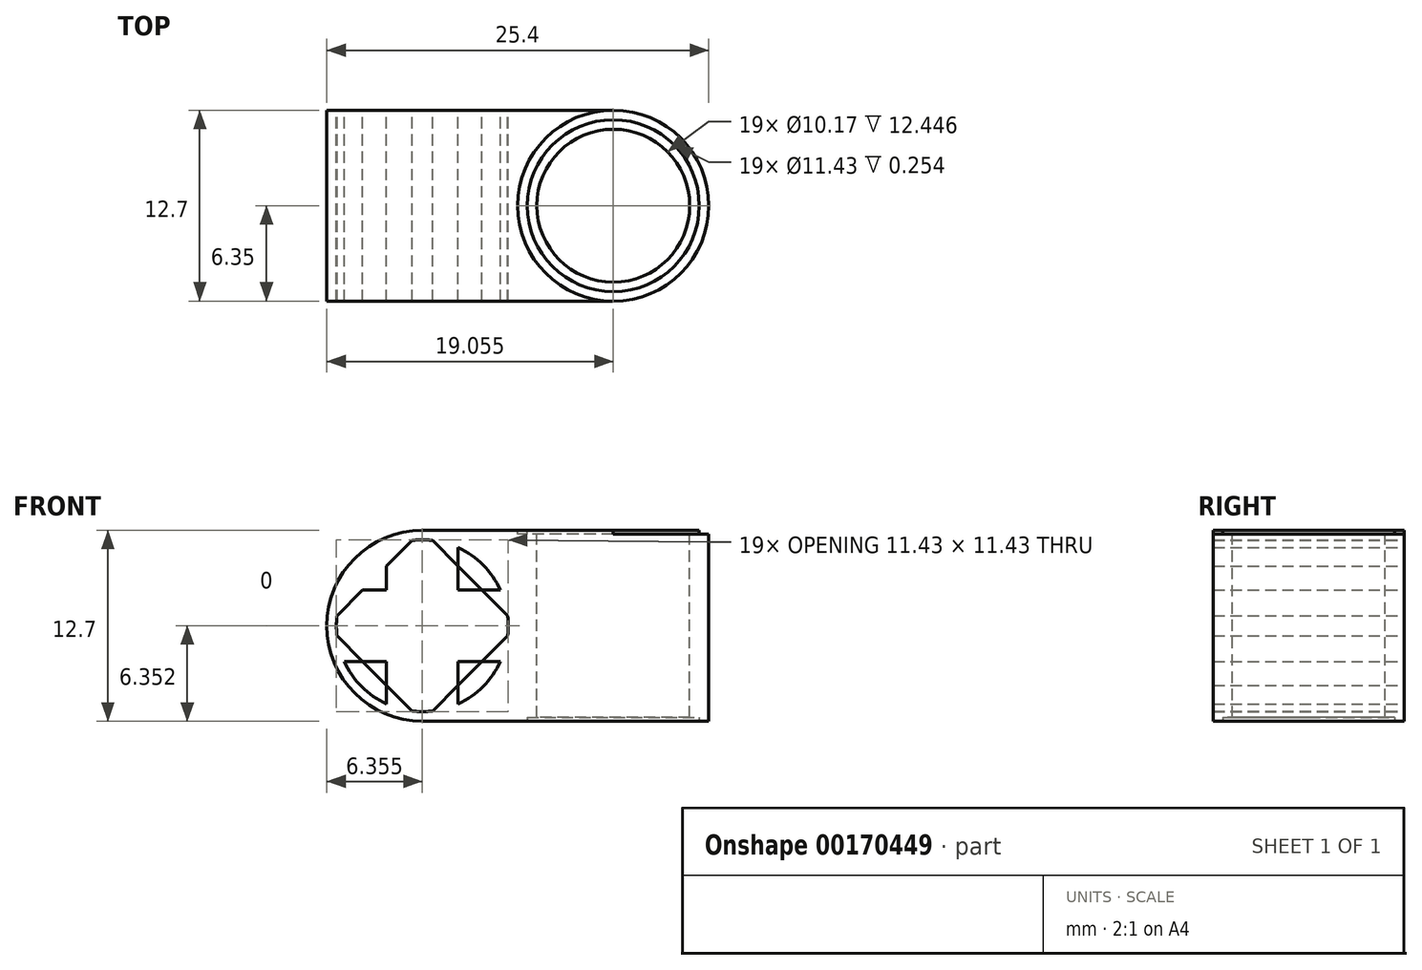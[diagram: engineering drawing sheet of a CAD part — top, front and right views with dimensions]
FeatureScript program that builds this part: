
annotation { "Feature Type Name" : "Feature", "Feature Type Description" : "" }
export const myFeature = defineFeature(function(context is Context, id is Id, definition is map)
    precondition{}
    {
        {
            var Q0;
            Q0=qCreatedBy(makeId("Front.planeOp"),FACE);
            var sketch = newSketch(context, id + "F0", { "sketchPlane" : qUnion([Q0])});
            skLineSegment(sketch, "E0.bottom", {"start": v(-13.88, 7.88) * mm, "end": v(11.52, 7.88) * mm});
            skLineSegment(sketch, "E0.top", {"start": v(-13.88, -4.82) * mm, "end": v(11.52, -4.82) * mm});
            skLineSegment(sketch, "E0.left", {"start": v(-13.88, 7.88) * mm, "end": v(-13.88, -4.82) * mm});
            skLineSegment(sketch, "E0.right", {"start": v(11.52, 7.88) * mm, "end": v(11.52, -4.82) * mm});
            skLineSegment(sketch, "E1", {"start": v(-1.18, 7.88) * mm, "end": v(-1.18, -4.82) * mm});
            skLineSegment(sketch, "E2", {"start": v(-13.88, 1.53) * mm, "end": v(-1.18, 1.53) * mm});
            skLineSegment(sketch, "E3", {"start": v(-7.53, -4.82) * mm, "end": v(-7.53, 7.88) * mm});
            skCircle(sketch, "E4", {"center": v(-7.53, 1.53) * mm, "radius": 6.35 * mm});
            skCircle(sketch, "E5", {"center": v(-7.53, 1.53) * mm, "radius": 5.72 * mm});
            skLineSegment(sketch, "E6", {"start": v(-7.53, 7.88) * mm, "end": v(-13.88, 1.53) * mm});
            skLineSegment(sketch, "E7", {"start": v(-9.11, 3.12) * mm, "end": v(-7.53, 4.7) * mm});
            skLineSegment(sketch, "E8", {"start": v(-7.53, 4.7) * mm, "end": v(-10.7, 1.53) * mm});
            skLineSegment(sketch, "E9", {"start": v(-9.11, 3.12) * mm, "end": v(-10.7, 4.7) * mm});
            skLineSegment(sketch, "E10", {"start": v(-9.9, 3.91) * mm, "end": v(-9.9, 6.73) * mm});
            skLineSegment(sketch, "E11", {"start": v(-9.9, 3.91) * mm, "end": v(-12.72, 3.91) * mm});
            skLineSegment(sketch, "E12", {"start": v(-7.53, 4.7) * mm, "end": v(-4.35, 1.53) * mm});
            skLineSegment(sketch, "E13", {"start": v(-7.53, 7.88) * mm, "end": v(-1.18, 1.53) * mm});
            skLineSegment(sketch, "E14", {"start": v(-5.94, 3.12) * mm, "end": v(-4.35, 4.7) * mm});
            skLineSegment(sketch, "E15", {"start": v(-5.14, 3.91) * mm, "end": v(-5.14, 6.73) * mm});
            skLineSegment(sketch, "E16", {"start": v(-5.14, 6.73) * mm, "end": v(-5.14, 3.91) * mm});
            skLineSegment(sketch, "E17", {"start": v(-5.14, 3.91) * mm, "end": v(-2.33, 3.91) * mm});
            skLineSegment(sketch, "E18", {"start": v(-10.7, 1.53) * mm, "end": v(-7.53, -1.64) * mm});
            skLineSegment(sketch, "E19", {"start": v(-7.53, -1.64) * mm, "end": v(-4.35, 1.53) * mm});
            skLineSegment(sketch, "E20", {"start": v(-13.88, 1.53) * mm, "end": v(-7.53, -4.82) * mm});
            skLineSegment(sketch, "E21", {"start": v(-7.53, -4.82) * mm, "end": v(-1.18, 1.53) * mm});
            skLineSegment(sketch, "E22", {"start": v(-9.11, -0.06) * mm, "end": v(-10.7, -1.64) * mm});
            skLineSegment(sketch, "E23", {"start": v(-5.94, -0.06) * mm, "end": v(-4.35, -1.64) * mm});
            skLineSegment(sketch, "E24", {"start": v(-5.14, -0.85) * mm, "end": v(-2.33, -0.85) * mm});
            skLineSegment(sketch, "E25", {"start": v(-2.33, -0.85) * mm, "end": v(-5.14, -0.85) * mm});
            skLineSegment(sketch, "E26", {"start": v(-5.14, -0.85) * mm, "end": v(-5.14, -3.66) * mm});
            skLineSegment(sketch, "E27", {"start": v(-9.9, -0.85) * mm, "end": v(-12.72, -0.85) * mm});
            skLineSegment(sketch, "E28", {"start": v(-12.72, -0.85) * mm, "end": v(-9.9, -0.85) * mm});
            skLineSegment(sketch, "E29", {"start": v(-9.9, -0.85) * mm, "end": v(-9.9, -3.66) * mm});
            skSolve(sketch);
        }
        {
            var Q0;
            {var subQ0=sQuery(id+"F0.wireOp",EDGE,"E1");var subQ1=sQuery(id+"F0.wireOp",EDGE,"E0.top");var subQ2=makeQuery(id+"F0.imprint","INTERSECT",VERTEX,{"derivedFrom":[subQ1,subQ0]});Q0=makeQuery(id+"F0.imprint","IMPRINT",FACE,{"disambiguationData":[TD([[makeQuery(id+"F0.imprint","IMPRINT",EDGE,{"disambiguationData":[TD([[subQ2,1.0]])],"derivedFrom":subQ1}),1.0]])]});}
            var Q1;
            {var subQ1=sQuery(id+"F0.wireOp",EDGE,"E2");var subQ3=sQuery(id+"F0.wireOp",EDGE,"E5");var subQ4=makeQuery(id+"F0.imprint","INTERSECT",VERTEX,{"disambiguationData":[OD(0.0)],"derivedFrom":[subQ1,subQ3]});Q1=makeQuery(id+"F0.imprint","IMPRINT",FACE,{"disambiguationData":[TD([[makeQuery(id+"F0.imprint","IMPRINT",EDGE,{"disambiguationData":[TD([[subQ4,1.0]])],"derivedFrom":subQ3}),-1.0]])]});}
            var Q2;
            {var subQ1=sQuery(id+"F0.wireOp",EDGE,"E2");var subQ3=sQuery(id+"F0.wireOp",EDGE,"E5");var subQ4=makeQuery(id+"F0.imprint","INTERSECT",VERTEX,{"disambiguationData":[OD(0.0)],"derivedFrom":[subQ1,subQ3]});Q2=makeQuery(id+"F0.imprint","IMPRINT",FACE,{"disambiguationData":[TD([[makeQuery(id+"F0.imprint","IMPRINT",EDGE,{"disambiguationData":[TD([[subQ4,-1.0]])],"derivedFrom":subQ3}),-1.0]])]});}
            var Q3;
            {var subQ1=sQuery(id+"F0.wireOp",EDGE,"E3");var subQ3=sQuery(id+"F0.wireOp",EDGE,"E5");var subQ4=makeQuery(id+"F0.imprint","INTERSECT",VERTEX,{"disambiguationData":[OD(0.0)],"derivedFrom":[subQ1,subQ3]});Q3=makeQuery(id+"F0.imprint","IMPRINT",FACE,{"disambiguationData":[TD([[makeQuery(id+"F0.imprint","IMPRINT",EDGE,{"disambiguationData":[TD([[subQ4,1.0]])],"derivedFrom":subQ3}),-1.0]])]});}
            var Q4;
            {var subQ1=sQuery(id+"F0.wireOp",EDGE,"E3");var subQ3=sQuery(id+"F0.wireOp",EDGE,"E5");var subQ4=makeQuery(id+"F0.imprint","INTERSECT",VERTEX,{"disambiguationData":[OD(0.0)],"derivedFrom":[subQ1,subQ3]});Q4=makeQuery(id+"F0.imprint","IMPRINT",FACE,{"disambiguationData":[TD([[makeQuery(id+"F0.imprint","IMPRINT",EDGE,{"disambiguationData":[TD([[subQ4,-1.0]])],"derivedFrom":subQ3}),-1.0]])]});}
            var Q5;
            {var subQ1=sQuery(id+"F0.wireOp",EDGE,"E3");var subQ3=sQuery(id+"F0.wireOp",EDGE,"E5");var subQ4=makeQuery(id+"F0.imprint","INTERSECT",VERTEX,{"disambiguationData":[OD(1.0)],"derivedFrom":[subQ1,subQ3]});Q5=makeQuery(id+"F0.imprint","IMPRINT",FACE,{"disambiguationData":[TD([[makeQuery(id+"F0.imprint","IMPRINT",EDGE,{"disambiguationData":[TD([[subQ4,1.0]])],"derivedFrom":subQ3}),-1.0]])]});}
            var Q6;
            {var subQ1=sQuery(id+"F0.wireOp",EDGE,"E3");var subQ3=sQuery(id+"F0.wireOp",EDGE,"E5");var subQ4=makeQuery(id+"F0.imprint","INTERSECT",VERTEX,{"disambiguationData":[OD(1.0)],"derivedFrom":[subQ1,subQ3]});Q6=makeQuery(id+"F0.imprint","IMPRINT",FACE,{"disambiguationData":[TD([[makeQuery(id+"F0.imprint","IMPRINT",EDGE,{"disambiguationData":[TD([[subQ4,-1.0]])],"derivedFrom":subQ3}),-1.0]])]});}
            var Q7;
            {var subQ0=sQuery(id+"F0.wireOp",EDGE,"E5");var subQ4=makeQuery(id+"F0.imprint","INTERSECT",VERTEX,{"derivedFrom":[subQ0,sQuery(id+"F0.wireOp",EDGE,"E17")]});Q7=makeQuery(id+"F0.imprint","IMPRINT",FACE,{"disambiguationData":[TD([[makeQuery(id+"F0.imprint","IMPRINT",EDGE,{"disambiguationData":[TD([[subQ4,1.0]])],"derivedFrom":subQ0}),-1.0]])]});}
            var Q8;
            {var subQ0=sQuery(id+"F0.wireOp",EDGE,"E5");var subQ4=makeQuery(id+"F0.imprint","INTERSECT",VERTEX,{"derivedFrom":[subQ0,sQuery(id+"F0.wireOp",EDGE,"E10")]});Q8=makeQuery(id+"F0.imprint","IMPRINT",FACE,{"disambiguationData":[TD([[makeQuery(id+"F0.imprint","IMPRINT",EDGE,{"disambiguationData":[TD([[subQ4,1.0]])],"derivedFrom":subQ0}),-1.0]])]});}
            var Q9;
            {var subQ0=sQuery(id+"F0.wireOp",EDGE,"E5");var subQ1=makeQuery(id+"F0.imprint","INTERSECT",VERTEX,{"derivedFrom":[subQ0,sQuery(id+"F0.wireOp",EDGE,"E28")]});Q9=makeQuery(id+"F0.imprint","IMPRINT",FACE,{"disambiguationData":[TD([[makeQuery(id+"F0.imprint","IMPRINT",EDGE,{"disambiguationData":[TD([[subQ1,1.0]])],"derivedFrom":subQ0}),-1.0]])]});}
            var Q10;
            {var subQ0=sQuery(id+"F0.wireOp",EDGE,"E5");var subQ4=makeQuery(id+"F0.imprint","INTERSECT",VERTEX,{"derivedFrom":[subQ0,sQuery(id+"F0.wireOp",EDGE,"E26")]});Q10=makeQuery(id+"F0.imprint","IMPRINT",FACE,{"disambiguationData":[TD([[makeQuery(id+"F0.imprint","IMPRINT",EDGE,{"disambiguationData":[TD([[subQ4,1.0]])],"derivedFrom":subQ0}),-1.0]])]});}
            var Q11;
            {var subQ0=sQuery(id+"F0.wireOp",EDGE,"E10");var subQ1=sQuery(id+"F0.wireOp",EDGE,"E5");var subQ2=makeQuery(id+"F0.imprint","INTERSECT",VERTEX,{"derivedFrom":[subQ1,subQ0]});Q11=makeQuery(id+"F0.imprint","IMPRINT",FACE,{"disambiguationData":[TD([[makeQuery(id+"F0.imprint","IMPRINT",EDGE,{"disambiguationData":[TD([[subQ2,-1.0]])],"derivedFrom":subQ1}),1.0]])]});}
            var Q12;
            {var subQ0=sQuery(id+"F0.wireOp",EDGE,"E9");var subQ1=sQuery(id+"F0.wireOp",EDGE,"E6");var subQ2=makeQuery(id+"F0.imprint","INTERSECT",VERTEX,{"derivedFrom":[subQ1,subQ0]});Q12=makeQuery(id+"F0.imprint","IMPRINT",FACE,{"disambiguationData":[TD([[makeQuery(id+"F0.imprint","IMPRINT",EDGE,{"disambiguationData":[TD([[subQ2,1.0]])],"derivedFrom":subQ1}),1.0]])]});}
            var Q13;
            {var subQ0=sQuery(id+"F0.wireOp",EDGE,"E9");var subQ1=sQuery(id+"F0.wireOp",EDGE,"E6");var subQ2=makeQuery(id+"F0.imprint","INTERSECT",VERTEX,{"derivedFrom":[subQ1,subQ0]});Q13=makeQuery(id+"F0.imprint","IMPRINT",FACE,{"disambiguationData":[TD([[makeQuery(id+"F0.imprint","IMPRINT",EDGE,{"disambiguationData":[TD([[subQ2,-1.0]])],"derivedFrom":subQ1}),1.0]])]});}
            var Q14;
            {var subQ0=sQuery(id+"F0.wireOp",EDGE,"E14");var subQ1=sQuery(id+"F0.wireOp",EDGE,"E13");var subQ2=makeQuery(id+"F0.imprint","INTERSECT",VERTEX,{"derivedFrom":[subQ1,subQ0]});Q14=makeQuery(id+"F0.imprint","IMPRINT",FACE,{"disambiguationData":[TD([[makeQuery(id+"F0.imprint","IMPRINT",EDGE,{"disambiguationData":[TD([[subQ2,1.0]])],"derivedFrom":subQ1}),-1.0]])]});}
            var Q15;
            {var subQ0=sQuery(id+"F0.wireOp",EDGE,"E16");var subQ1=sQuery(id+"F0.wireOp",EDGE,"E5");var subQ2=makeQuery(id+"F0.imprint","INTERSECT",VERTEX,{"derivedFrom":[subQ1,subQ0]});Q15=makeQuery(id+"F0.imprint","IMPRINT",FACE,{"disambiguationData":[TD([[makeQuery(id+"F0.imprint","IMPRINT",EDGE,{"disambiguationData":[TD([[subQ2,1.0]])],"derivedFrom":subQ1}),1.0]])]});}
            var Q16;
            {var subQ0=sQuery(id+"F0.wireOp",EDGE,"E14");var subQ1=sQuery(id+"F0.wireOp",EDGE,"E13");var subQ2=makeQuery(id+"F0.imprint","INTERSECT",VERTEX,{"derivedFrom":[subQ1,subQ0]});Q16=makeQuery(id+"F0.imprint","IMPRINT",FACE,{"disambiguationData":[TD([[makeQuery(id+"F0.imprint","IMPRINT",EDGE,{"disambiguationData":[TD([[subQ2,-1.0]])],"derivedFrom":subQ1}),-1.0]])]});}
            var Q17;
            {var subQ0=sQuery(id+"F0.wireOp",EDGE,"E25");var subQ1=sQuery(id+"F0.wireOp",EDGE,"E5");var subQ2=makeQuery(id+"F0.imprint","INTERSECT",VERTEX,{"derivedFrom":[subQ1,subQ0]});Q17=makeQuery(id+"F0.imprint","IMPRINT",FACE,{"disambiguationData":[TD([[makeQuery(id+"F0.imprint","IMPRINT",EDGE,{"disambiguationData":[TD([[subQ2,1.0]])],"derivedFrom":subQ1}),1.0]])]});}
            var Q18;
            {var subQ0=sQuery(id+"F0.wireOp",EDGE,"E23");var subQ1=sQuery(id+"F0.wireOp",EDGE,"E21");var subQ2=makeQuery(id+"F0.imprint","INTERSECT",VERTEX,{"derivedFrom":[subQ1,subQ0]});Q18=makeQuery(id+"F0.imprint","IMPRINT",FACE,{"disambiguationData":[TD([[makeQuery(id+"F0.imprint","IMPRINT",EDGE,{"disambiguationData":[TD([[subQ2,-1.0]])],"derivedFrom":subQ1}),1.0]])]});}
            var Q19;
            {var subQ0=sQuery(id+"F0.wireOp",EDGE,"E23");var subQ1=sQuery(id+"F0.wireOp",EDGE,"E21");var subQ2=makeQuery(id+"F0.imprint","INTERSECT",VERTEX,{"derivedFrom":[subQ1,subQ0]});Q19=makeQuery(id+"F0.imprint","IMPRINT",FACE,{"disambiguationData":[TD([[makeQuery(id+"F0.imprint","IMPRINT",EDGE,{"disambiguationData":[TD([[subQ2,1.0]])],"derivedFrom":subQ1}),1.0]])]});}
            var Q20;
            {var subQ4=sQuery(id+"F0.wireOp",EDGE,"E28");var subQ6=sQuery(id+"F0.wireOp",EDGE,"E5");var subQ8=makeQuery(id+"F0.imprint","INTERSECT",VERTEX,{"derivedFrom":[subQ6,subQ4]});Q20=makeQuery(id+"F0.imprint","IMPRINT",FACE,{"disambiguationData":[TD([[makeQuery(id+"F0.imprint","IMPRINT",EDGE,{"disambiguationData":[TD([[subQ8,-1.0]])],"derivedFrom":subQ6}),1.0]])]});}
            var Q21;
            {var subQ0=sQuery(id+"F0.wireOp",EDGE,"E22");var subQ1=sQuery(id+"F0.wireOp",EDGE,"E20");var subQ2=makeQuery(id+"F0.imprint","INTERSECT",VERTEX,{"derivedFrom":[subQ1,subQ0]});Q21=makeQuery(id+"F0.imprint","IMPRINT",FACE,{"disambiguationData":[TD([[makeQuery(id+"F0.imprint","IMPRINT",EDGE,{"disambiguationData":[TD([[subQ2,-1.0]])],"derivedFrom":subQ1}),1.0]])]});}
            var Q22;
            {var subQ0=sQuery(id+"F0.wireOp",EDGE,"E22");var subQ1=sQuery(id+"F0.wireOp",EDGE,"E20");var subQ2=makeQuery(id+"F0.imprint","INTERSECT",VERTEX,{"derivedFrom":[subQ1,subQ0]});Q22=makeQuery(id+"F0.imprint","IMPRINT",FACE,{"disambiguationData":[TD([[makeQuery(id+"F0.imprint","IMPRINT",EDGE,{"disambiguationData":[TD([[subQ2,1.0]])],"derivedFrom":subQ1}),1.0]])]});}
            var Q23;
            {var subQ1=sQuery(id+"F0.wireOp",EDGE,"E2");var subQ3=sQuery(id+"F0.wireOp",EDGE,"E5");var subQ4=makeQuery(id+"F0.imprint","INTERSECT",VERTEX,{"disambiguationData":[OD(1.0)],"derivedFrom":[subQ1,subQ3]});Q23=makeQuery(id+"F0.imprint","IMPRINT",FACE,{"disambiguationData":[TD([[makeQuery(id+"F0.imprint","IMPRINT",EDGE,{"disambiguationData":[TD([[subQ4,-1.0]])],"derivedFrom":subQ3}),-1.0]])]});}
            var Q24;
            {var subQ1=sQuery(id+"F0.wireOp",EDGE,"E2");var subQ3=sQuery(id+"F0.wireOp",EDGE,"E5");var subQ4=makeQuery(id+"F0.imprint","INTERSECT",VERTEX,{"disambiguationData":[OD(1.0)],"derivedFrom":[subQ1,subQ3]});Q24=makeQuery(id+"F0.imprint","IMPRINT",FACE,{"disambiguationData":[TD([[makeQuery(id+"F0.imprint","IMPRINT",EDGE,{"disambiguationData":[TD([[subQ4,1.0]])],"derivedFrom":subQ3}),-1.0]])]});}
            var Q25;
            {var subQ0=sQuery(id+"F0.wireOp",EDGE,"E1");var subQ1=sQuery(id+"F0.wireOp",EDGE,"E0.bottom");var subQ2=makeQuery(id+"F0.imprint","INTERSECT",VERTEX,{"derivedFrom":[subQ1,subQ0]});Q25=makeQuery(id+"F0.imprint","IMPRINT",FACE,{"disambiguationData":[TD([[makeQuery(id+"F0.imprint","IMPRINT",EDGE,{"disambiguationData":[TD([[subQ2,1.0]])],"derivedFrom":subQ1}),-1.0]])]});}
            var Q26;
            {var subQ4=sQuery(id+"F0.wireOp",EDGE,"E0.right");Q26=makeQuery(id+"F0.imprint","IMPRINT",FACE,{"disambiguationData":[TD([[makeQuery(id+"F0.imprint","IMPRINT",EDGE,{"derivedFrom":subQ4}),-1.0]])]});}
            extrude(context, id + "F1", {"entities" : qUnion([Q0, Q1, Q2, Q3, Q4, Q5, Q6, Q7, Q8, Q9, Q10, Q11, Q12, Q13, Q14, Q15, Q16, Q17, Q18, Q19, Q20, Q21, Q22, Q23, Q24, Q25, Q26]), "depth" : 12.7 * mm});
        }
        {
            var Q0;
            Q0=makeQuery(id+"F1.opExtrude","SWEPT_FACE",FACE,{"disambiguationData":[OSD([sQuery(id+"F0.wireOp",EDGE,"E0.bottom")])]});
            var sketch = newSketch(context, id + "F2", { "sketchPlane" : qUnion([Q0])});
            skLineSegment(sketch, "E30.bottom", {"start": v(-13.88, 0) * mm, "end": v(11.52, 0) * mm});
            skLineSegment(sketch, "E30.top", {"start": v(-13.88, -12.7) * mm, "end": v(11.52, -12.7) * mm});
            skLineSegment(sketch, "E30.left", {"start": v(-13.88, 0) * mm, "end": v(-13.88, -12.7) * mm});
            skLineSegment(sketch, "E30.right", {"start": v(11.52, 0) * mm, "end": v(11.52, -12.7) * mm});
            skLineSegment(sketch, "E31", {"start": v(-1.18, 0) * mm, "end": v(-1.18, -12.7) * mm});
            skLineSegment(sketch, "E32", {"start": v(5.17, 0) * mm, "end": v(5.17, -12.7) * mm});
            skCircle(sketch, "E33", {"center": v(5.17, -6.35) * mm, "radius": 6.35 * mm});
            skCircle(sketch, "E34", {"center": v(5.17, -6.35) * mm, "radius": 5.72 * mm});
            skCircle(sketch, "E35", {"center": v(5.17, -6.35) * mm, "radius": 5.08 * mm});
            skSolve(sketch);
        }
        {
            var Q0;
            {var subQ0=sQuery(id+"F2.wireOp",EDGE,"E30.right");var subQ1=sQuery(id+"F2.wireOp",EDGE,"E30.bottom");var subQ2=makeQuery(id+"F2.imprint","INTERSECT",VERTEX,{"derivedFrom":[subQ1,subQ0]});Q0=makeQuery(id+"F2.imprint","IMPRINT",FACE,{"disambiguationData":[TD([[makeQuery(id+"F2.imprint","IMPRINT",EDGE,{"disambiguationData":[TD([[subQ2,1.0]])],"derivedFrom":subQ0}),1.0]])]});}
            var Q1;
            {var subQ0=sQuery(id+"F2.wireOp",EDGE,"E30.right");var subQ1=sQuery(id+"F2.wireOp",EDGE,"E30.top");var subQ2=makeQuery(id+"F2.imprint","INTERSECT",VERTEX,{"derivedFrom":[subQ1,subQ0]});Q1=makeQuery(id+"F2.imprint","IMPRINT",FACE,{"disambiguationData":[TD([[makeQuery(id+"F2.imprint","IMPRINT",EDGE,{"disambiguationData":[TD([[subQ2,-1.0]])],"derivedFrom":subQ0}),1.0]])]});}
            var Q2;
            {var subQ0=sQuery(id+"F2.wireOp",EDGE,"E35");var subQ1=sQuery(id+"F2.wireOp",EDGE,"E32");var subQ2=makeQuery(id+"F2.imprint","INTERSECT",VERTEX,{"disambiguationData":[OD(0.0)],"derivedFrom":[subQ1,subQ0]});Q2=makeQuery(id+"F2.imprint","IMPRINT",FACE,{"disambiguationData":[TD([[makeQuery(id+"F2.imprint","IMPRINT",EDGE,{"disambiguationData":[TD([[subQ2,-1.0]])],"derivedFrom":subQ1}),-1.0]])]});}
            var Q3;
            {var subQ0=sQuery(id+"F2.wireOp",EDGE,"E35");var subQ1=sQuery(id+"F2.wireOp",EDGE,"E32");var subQ2=makeQuery(id+"F2.imprint","INTERSECT",VERTEX,{"disambiguationData":[OD(0.0)],"derivedFrom":[subQ1,subQ0]});Q3=makeQuery(id+"F2.imprint","IMPRINT",FACE,{"disambiguationData":[TD([[makeQuery(id+"F2.imprint","IMPRINT",EDGE,{"disambiguationData":[TD([[subQ2,-1.0]])],"derivedFrom":subQ1}),1.0]])]});}
            extrude(context, id + "F3", {"entities" : qUnion([Q0, Q1, Q2, Q3]), "operationType" : NewBodyOperationType.REMOVE, "oppositeDirection" : true, "depth" : 12.7 * mm});
        }
        {
            var Q0;
            {var subQ0=sQuery(id+"F2.wireOp",EDGE,"E34");var subQ1=sQuery(id+"F2.wireOp",EDGE,"E32");var subQ2=makeQuery(id+"F2.imprint","INTERSECT",VERTEX,{"disambiguationData":[OD(0.0)],"derivedFrom":[subQ1,subQ0]});Q0=makeQuery(id+"F2.imprint","IMPRINT",FACE,{"disambiguationData":[TD([[makeQuery(id+"F2.imprint","IMPRINT",EDGE,{"disambiguationData":[TD([[subQ2,-1.0]])],"derivedFrom":subQ1}),-1.0]])]});}
            var Q1;
            {var subQ0=sQuery(id+"F2.wireOp",EDGE,"E34");var subQ1=sQuery(id+"F2.wireOp",EDGE,"E32");var subQ2=makeQuery(id+"F2.imprint","INTERSECT",VERTEX,{"disambiguationData":[OD(0.0)],"derivedFrom":[subQ1,subQ0]});Q1=makeQuery(id+"F2.imprint","IMPRINT",FACE,{"disambiguationData":[TD([[makeQuery(id+"F2.imprint","IMPRINT",EDGE,{"disambiguationData":[TD([[subQ2,-1.0]])],"derivedFrom":subQ1}),1.0]])]});}
            extrude(context, id + "F4", {"entities" : qUnion([Q0, Q1]), "operationType" : NewBodyOperationType.REMOVE, "oppositeDirection" : true, "depth" : 0.25 * mm});
        }
        {
            var Q0;
            Q0=makeQuery(id+"F1.opExtrude","SWEPT_FACE",FACE,{"disambiguationData":[OSD([sQuery(id+"F0.wireOp",EDGE,"E0.top")])]});
            var sketch = newSketch(context, id + "F5", { "sketchPlane" : qUnion([Q0])});
            skCircle(sketch, "E36", {"center": v(5.17, 6.35) * mm, "radius": 5.08 * mm});
            skCircle(sketch, "E37", {"center": v(5.17, 6.35) * mm, "radius": 5.72 * mm});
            skCircle(sketch, "E38", {"center": v(5.17, 6.35) * mm, "radius": 6.35 * mm});
            skSolve(sketch);
        }
        {
            var Q0;
            Q0=makeQuery(id+"F5.imprint","IMPRINT",FACE,{"disambiguationData":[TD([[makeQuery(id+"F5.imprint","IMPRINT",EDGE,{"derivedFrom":sQuery(id+"F5.wireOp",EDGE,"E37")}),1.0]])]});
            extrude(context, id + "F6", {"entities" : qUnion([Q0]), "operationType" : NewBodyOperationType.REMOVE, "oppositeDirection" : true, "depth" : 0.25 * mm});
        }
    });
